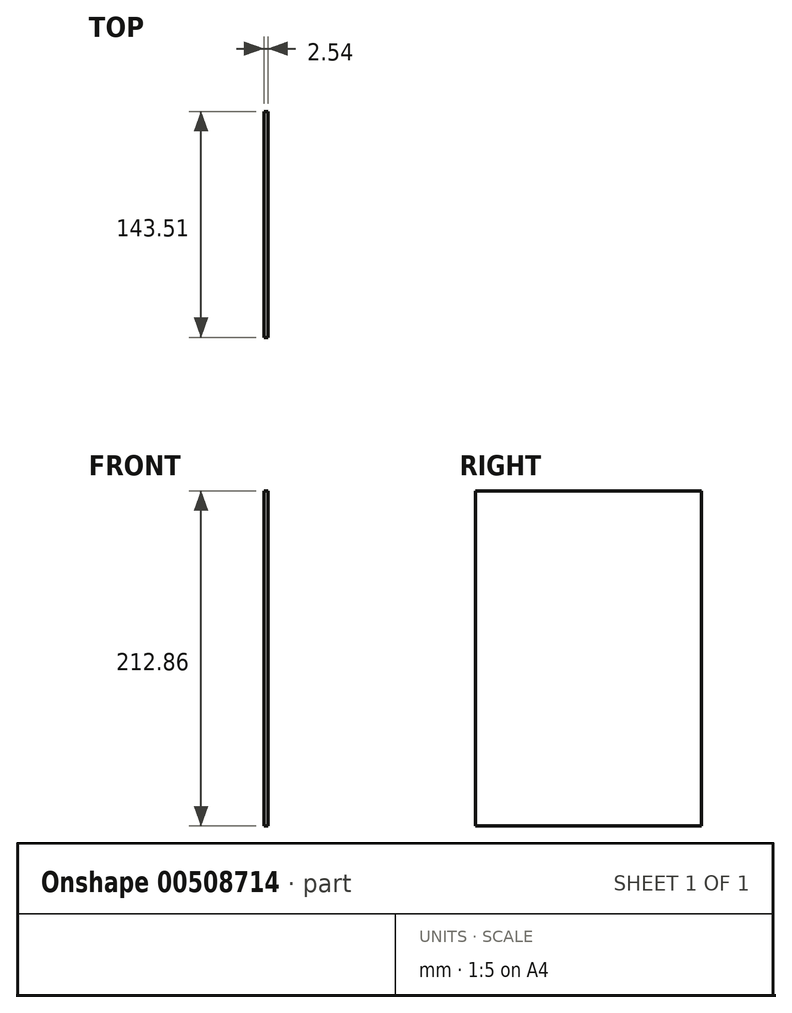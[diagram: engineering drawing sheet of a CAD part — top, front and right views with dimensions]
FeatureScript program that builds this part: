
annotation { "Feature Type Name" : "Feature", "Feature Type Description" : "" }
export const myFeature = defineFeature(function(context is Context, id is Id, definition is map)
    precondition{}
    {
        {
            var Q0;
            Q0=qCreatedBy(makeId("Front.planeOp"),FACE);
            var sketch = newSketch(context, id + "F0", { "sketchPlane" : qUnion([Q0])});
            skLineSegment(sketch, "E0", {"start": v(-71.42, -65.59) * mm, "end": v(-68.88, -65.59) * mm});
            skLineSegment(sketch, "E1", {"start": v(-68.88, -65.59) * mm, "end": v(-68.88, 147.27) * mm});
            skLineSegment(sketch, "E2", {"start": v(-68.88, 147.27) * mm, "end": v(-71.42, 147.27) * mm});
            skLineSegment(sketch, "E3", {"start": v(-71.42, 147.27) * mm, "end": v(-71.42, -65.59) * mm});
            skSolve(sketch);
        }
        {
            var Q0;
            Q0=makeQuery(id+"F0.imprint","IMPRINT",FACE,{"disambiguationData":[TD([[makeQuery(id+"F0.imprint","IMPRINT",EDGE,{"derivedFrom":sQuery(id+"F0.wireOp",EDGE,"E0")}),1.0]])]});
            extrude(context, id + "F1", {"entities" : qUnion([Q0]), "depth" : 143.5 * mm});
        }
    });
